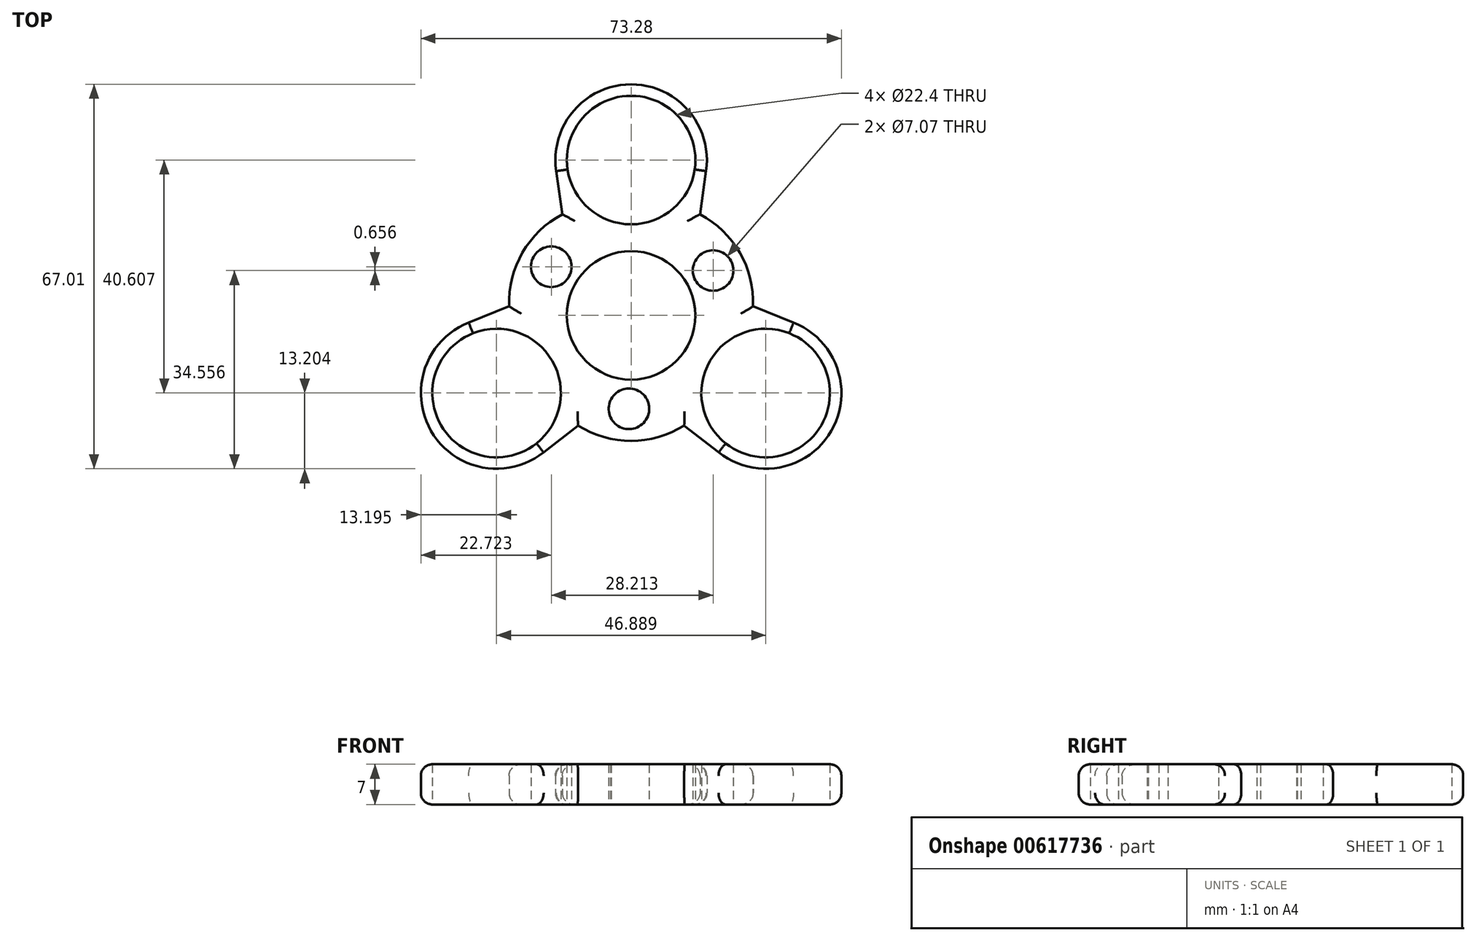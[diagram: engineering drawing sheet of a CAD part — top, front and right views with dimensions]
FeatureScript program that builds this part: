
annotation { "Feature Type Name" : "Feature", "Feature Type Description" : "" }
export const myFeature = defineFeature(function(context is Context, id is Id, definition is map)
    precondition{}
    {
        {
            var Q0;
            Q0=qCreatedBy(makeId("Top.planeOp"),FACE);
            var sketch = newSketch(context, id + "F0", { "sketchPlane" : qUnion([Q0])});
            skCircle(sketch, "E0", {"center": v(0, 0) * mm, "radius": 11.2 * mm});
            skCircle(sketch, "E1", {"center": v(0, 27.07) * mm, "radius": 11.2 * mm});
            skArc(sketch, "E2", {"start": v(13.06, 25.14) * mm, "mid": v(0, 40.27) * mm, "end": v(-13.06, 25.14) * mm});
            skPoint(sketch, "E3.center", {"position": v(-0.21, -0.24) * mm});
            skCircle(sketch, "E4.1.0", {"center": v(-23.44, -13.54) * mm, "radius": 11.2 * mm});
            skArc(sketch, "E4.1.1", {"start": v(-28.3, -1.26) * mm, "mid": v(-34.88, -20.14) * mm, "end": v(-15.24, -23.88) * mm});
            skCircle(sketch, "E4.2.0", {"center": v(23.44, -13.54) * mm, "radius": 11.2 * mm});
            skArc(sketch, "E4.2.1", {"start": v(15.24, -23.88) * mm, "mid": v(34.88, -20.14) * mm, "end": v(28.3, -1.26) * mm});
            skPoint(sketch, "E5.orphan", {"position": v(-30.07, -2.12) * mm});
            skLineSegment(sketch, "E6", {"start": v(16.77, 10.34) * mm, "end": v(17.34, 9.35) * mm});
            skLineSegment(sketch, "E7", {"start": v(-3.44, -14.52) * mm, "end": v(-3.25, -14.52) * mm});
            skLineSegment(sketch, "E8.MirrorCS", {"start": v(-3.25, -14.52) * mm, "end": v(-3.6, -14.8) * mm});
            skLineSegment(sketch, "E9.1.0", {"start": v(21.25, 1.6) * mm, "end": v(28.3, -1.26) * mm});
            skLineSegment(sketch, "E9.2.0", {"start": v(-12, 17.6) * mm, "end": v(-13.06, 25.14) * mm});
            skLineSegment(sketch, "E10.1.0", {"start": v(14.3, 4.28) * mm, "end": v(14.2, 4.45) * mm});
            skLineSegment(sketch, "E10.2.0", {"start": v(-10.86, 10.24) * mm, "end": v(-10.95, 10.07) * mm});
            skPoint(sketch, "E11.startSnap0", {"position": v(-9.25, -19.2) * mm});
            skPoint(sketch, "E12.startSnap0", {"position": v(-12, 17.6) * mm});
            skArc(sketch, "E13", {"start": v(21.25, 1.6) * mm, "mid": v(18.94, 10.93) * mm, "end": v(12, 17.6) * mm});
            skLineSegment(sketch, "E14.trimOffspring", {"start": v(12, 17.6) * mm, "end": v(13.06, 25.14) * mm});
            skPoint(sketch, "E15.orphan", {"position": v(14.2, 4.45) * mm});
            skArc(sketch, "E16.1.1", {"start": v(-12, 17.6) * mm, "mid": v(-18.94, 10.93) * mm, "end": v(-21.25, 1.6) * mm});
            skArc(sketch, "E16.2.1", {"start": v(-9.25, -19.2) * mm, "mid": v(0, -21.87) * mm, "end": v(9.25, -19.2) * mm});
            skPoint(sketch, "E17.orphan", {"position": v(-10.95, 10.07) * mm});
            skLineSegment(sketch, "E18.trimOffspring", {"start": v(-21.25, 1.6) * mm, "end": v(-28.3, -1.26) * mm});
            skPoint(sketch, "E19.end.orphan", {"position": v(-17.34, 9.35) * mm});
            skPoint(sketch, "E19.start.orphan", {"position": v(-16.77, 10.34) * mm});
            skPoint(sketch, "E20.orphan", {"position": v(-14.2, 4.45) * mm});
            skPoint(sketch, "E21.end.orphan", {"position": v(-0.57, -19.7) * mm});
            skPoint(sketch, "E21.start.orphan", {"position": v(0.57, -19.7) * mm});
            skLineSegment(sketch, "E22.2.2", {"start": v(-3.44, -14.52) * mm, "end": v(-3.6, -14.8) * mm});
            skLineSegment(sketch, "E23.trimOffspring", {"start": v(-9.25, -19.2) * mm, "end": v(-15.24, -23.88) * mm});
            skLineSegment(sketch, "E24.trimOffspring", {"start": v(9.25, -19.2) * mm, "end": v(15.24, -23.88) * mm});
            skPoint(sketch, "E25.end.orphan", {"position": v(16.77, 4.28) * mm});
            skPoint(sketch, "E26.orphan", {"position": v(10.95, 10.07) * mm});
            skPoint(sketch, "E27.orphan", {"position": v(3.25, -14.52) * mm});
            skPoint(sketch, "E28.orphan", {"position": v(-4.68, -16.67) * mm});
            skCircle(sketch, "E29", {"center": v(14.3, 7.82) * mm, "radius": 3.54 * mm});
            skCircle(sketch, "E30.1.0", {"center": v(-13.92, 8.47) * mm, "radius": 3.54 * mm});
            skCircle(sketch, "E30.2.0", {"center": v(-0.38, -16.29) * mm, "radius": 3.54 * mm});
            skSolve(sketch);
        }
        {
            var Q0;
            Q0 = qSketchRegion(id + "F0", true);
            extrude(context, id + "F1", {"entities" : qUnion([Q0]), "depth" : 7 * mm, "offsetDistance" : 25 * mm});
        }
        {
            var Q0;
            Q0=makeQuery(id+"F1.opExtrude","CAP_EDGE",EDGE,{"disambiguationData":[OSD([sQuery(id+"F0.wireOp",EDGE,"E16.1.1")])],"isStart":false});
            var Q1;
            Q1=makeQuery(id+"F1.opExtrude","CAP_EDGE",EDGE,{"disambiguationData":[OSD([sQuery(id+"F0.wireOp",EDGE,"E16.1.1")])],"isStart":true});
            var Q2;
            Q2=makeQuery(id+"F1.opExtrude","CAP_EDGE",EDGE,{"disambiguationData":[OSD([sQuery(id+"F0.wireOp",EDGE,"E16.2.1")])],"isStart":true});
            var Q3;
            Q3=makeQuery(id+"F1.opExtrude","CAP_EDGE",EDGE,{"disambiguationData":[OSD([sQuery(id+"F0.wireOp",EDGE,"E13")])],"isStart":true});
            var Q4;
            Q4=makeQuery(id+"F1.opExtrude","CAP_EDGE",EDGE,{"disambiguationData":[OSD([sQuery(id+"F0.wireOp",EDGE,"E13")])],"isStart":false});
            var Q5;
            Q5=makeQuery(id+"F1.opExtrude","CAP_EDGE",EDGE,{"disambiguationData":[OSD([sQuery(id+"F0.wireOp",EDGE,"E16.2.1")])],"isStart":false});
            fillet(context, id + "F2", {"entities" : qUnion([Q0, Q1, Q2, Q3, Q4, Q5]), "radius" : 2 * mm, "tangentPropagation" : true, "allowEdgeOverflow" : false});
        }
        {
            var Q0;
            Q0=makeQuery(id+"F1.opExtrude","CAP_EDGE",EDGE,{"disambiguationData":[OSD([sQuery(id+"F0.wireOp",EDGE,"E14.trimOffspring")])],"isStart":true});
            var Q1;
            Q1=makeQuery(id+"F1.opExtrude","CAP_EDGE",EDGE,{"disambiguationData":[OSD([sQuery(id+"F0.wireOp",EDGE,"E14.trimOffspring")])],"isStart":false});
            var Q2;
            Q2=makeQuery(id+"F1.opExtrude","CAP_EDGE",EDGE,{"disambiguationData":[OSD([sQuery(id+"F0.wireOp",EDGE,"E2")])],"isStart":true});
            var Q3;
            Q3=makeQuery(id+"F1.opExtrude","CAP_EDGE",EDGE,{"disambiguationData":[OSD([sQuery(id+"F0.wireOp",EDGE,"E2")])],"isStart":false});
            var Q4;
            Q4=makeQuery(id+"F1.opExtrude","CAP_EDGE",EDGE,{"disambiguationData":[OSD([sQuery(id+"F0.wireOp",EDGE,"E18.trimOffspring")])],"isStart":false});
            var Q5;
            Q5=makeQuery(id+"F1.opExtrude","CAP_EDGE",EDGE,{"disambiguationData":[OSD([sQuery(id+"F0.wireOp",EDGE,"E18.trimOffspring")])],"isStart":true});
            var Q6;
            Q6=makeQuery(id+"F1.opExtrude","CAP_EDGE",EDGE,{"disambiguationData":[OSD([sQuery(id+"F0.wireOp",EDGE,"E4.1.1")])],"isStart":true});
            var Q7;
            Q7=makeQuery(id+"F1.opExtrude","CAP_EDGE",EDGE,{"disambiguationData":[OSD([sQuery(id+"F0.wireOp",EDGE,"E4.1.1")])],"isStart":false});
            var Q8;
            Q8=makeQuery(id+"F1.opExtrude","CAP_EDGE",EDGE,{"disambiguationData":[OSD([sQuery(id+"F0.wireOp",EDGE,"E9.1.0")])],"isStart":false});
            var Q9;
            Q9=makeQuery(id+"F1.opExtrude","CAP_EDGE",EDGE,{"disambiguationData":[OSD([sQuery(id+"F0.wireOp",EDGE,"E9.1.0")])],"isStart":true});
            var Q10;
            Q10=makeQuery(id+"F1.opExtrude","CAP_EDGE",EDGE,{"disambiguationData":[OSD([sQuery(id+"F0.wireOp",EDGE,"E4.2.1")])],"isStart":true});
            var Q11;
            Q11=makeQuery(id+"F1.opExtrude","CAP_EDGE",EDGE,{"disambiguationData":[OSD([sQuery(id+"F0.wireOp",EDGE,"E4.2.1")])],"isStart":false});
            fillet(context, id + "F3", {"entities" : qUnion([Q0, Q1, Q2, Q3, Q4, Q5, Q6, Q7, Q8, Q9, Q10, Q11]), "radius" : 2 * mm, "tangentPropagation" : true, "allowEdgeOverflow" : false});
        }
    });
